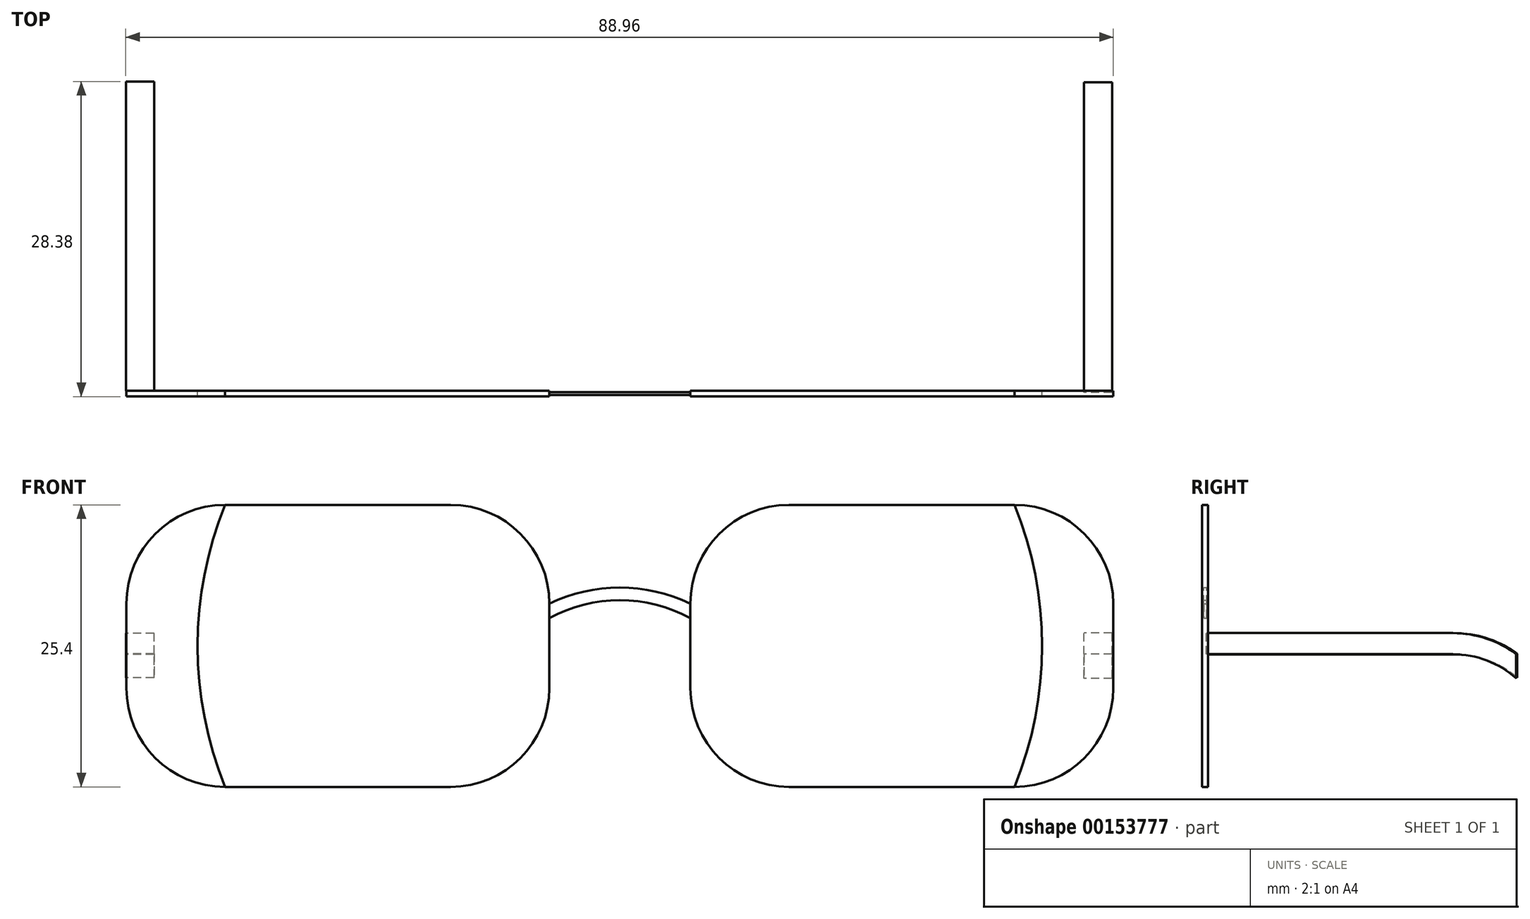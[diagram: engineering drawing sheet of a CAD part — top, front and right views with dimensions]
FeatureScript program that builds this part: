
annotation { "Feature Type Name" : "Feature", "Feature Type Description" : "" }
export const myFeature = defineFeature(function(context is Context, id is Id, definition is map)
    precondition{}
    {
        {
            var Q0;
            Q0=qCreatedBy(makeId("Front.planeOp"),FACE);
            var sketch = newSketch(context, id + "F0", { "sketchPlane" : qUnion([Q0])});
            skLineSegment(sketch, "E0.bottom", {"start": v(-55.76, 55.32) * mm, "end": v(-35.44, 55.32) * mm});
            skLineSegment(sketch, "E0.top", {"start": v(-55.76, 29.92) * mm, "end": v(-35.44, 29.92) * mm});
            skLineSegment(sketch, "E0.left", {"start": v(-64.65, 46.43) * mm, "end": v(-64.65, 38.8) * mm});
            skLineSegment(sketch, "E0.right", {"start": v(-26.55, 46.43) * mm, "end": v(-26.55, 38.8) * mm});
            skLineSegment(sketch, "E1", {"start": v(-13.85, 46.43) * mm, "end": v(-13.85, 38.8) * mm});
            skLineSegment(sketch, "E2", {"start": v(-4.96, 29.92) * mm, "end": v(15.36, 29.92) * mm});
            skLineSegment(sketch, "E3", {"start": v(24.25, 38.8) * mm, "end": v(24.25, 46.43) * mm});
            skLineSegment(sketch, "E4", {"start": v(15.36, 55.32) * mm, "end": v(-4.96, 55.32) * mm});
            skPoint(sketch, "E5.visualSharp", {"position": v(-64.65, 55.32) * mm});
            skArc(sketch, "E5.filletArc", {"start": v(-55.76, 55.32) * mm, "mid": v(-62.05, 52.71) * mm, "end": v(-64.65, 46.43) * mm});
            skPoint(sketch, "E6.visualSharp", {"position": v(-64.65, 29.92) * mm});
            skArc(sketch, "E6.filletArc", {"start": v(-64.65, 38.8) * mm, "mid": v(-62.05, 32.52) * mm, "end": v(-55.76, 29.92) * mm});
            skPoint(sketch, "E7.visualSharp", {"position": v(-26.55, 29.92) * mm});
            skArc(sketch, "E7.filletArc", {"start": v(-35.44, 29.92) * mm, "mid": v(-29.16, 32.52) * mm, "end": v(-26.55, 38.8) * mm});
            skPoint(sketch, "E8.visualSharp", {"position": v(-26.55, 55.32) * mm});
            skArc(sketch, "E8.filletArc", {"start": v(-26.55, 46.43) * mm, "mid": v(-29.16, 52.71) * mm, "end": v(-35.44, 55.32) * mm});
            skPoint(sketch, "E9.visualSharp", {"position": v(24.25, 55.32) * mm});
            skArc(sketch, "E9.filletArc", {"start": v(24.25, 54.68) * mm, "mid": v(24.06, 55.13) * mm, "end": v(23.61, 55.32) * mm});
            skPoint(sketch, "E10.visualSharp", {"position": v(-13.85, 55.32) * mm});
            skArc(sketch, "E10.filletArc", {"start": v(-4.96, 55.32) * mm, "mid": v(-11.25, 52.71) * mm, "end": v(-13.85, 46.43) * mm});
            skPoint(sketch, "E11.visualSharp", {"position": v(-13.85, 29.92) * mm});
            skArc(sketch, "E11.filletArc", {"start": v(-13.85, 38.8) * mm, "mid": v(-11.25, 32.52) * mm, "end": v(-4.96, 29.92) * mm});
            skPoint(sketch, "E12.visualSharp", {"position": v(24.25, 29.92) * mm});
            skArc(sketch, "E12.filletArc", {"start": v(15.36, 29.92) * mm, "mid": v(21.64, 32.52) * mm, "end": v(24.25, 38.8) * mm});
            skArc(sketch, "E13.filletArc", {"start": v(24.25, 46.43) * mm, "mid": v(21.64, 52.71) * mm, "end": v(15.36, 55.32) * mm});
            skArc(sketch, "E14", {"start": v(15.36, 29.92) * mm, "mid": v(17.83, 42.62) * mm, "end": v(15.36, 55.32) * mm});
            skArc(sketch, "E15", {"start": v(-55.76, 55.32) * mm, "mid": v(-58.24, 42.62) * mm, "end": v(-55.76, 29.92) * mm});
            skArc(sketch, "E16", {"start": v(-13.85, 46.43) * mm, "mid": v(-20.2, 47.87) * mm, "end": v(-26.55, 46.43) * mm});
            skPoint(sketch, "E17", {"position": v(-26.55, 45.13) * mm});
            skPoint(sketch, "E18", {"position": v(-13.85, 45.13) * mm});
            skArc(sketch, "E19", {"start": v(-13.85, 45.13) * mm, "mid": v(-20.2, 46.73) * mm, "end": v(-26.55, 45.13) * mm});
            skSolve(sketch);
        }
        {
            var Q0;
            Q0=makeQuery(id+"F0.imprint","IMPRINT",FACE,{"disambiguationData":[TD([[makeQuery(id+"F0.imprint","IMPRINT",EDGE,{"derivedFrom":sQuery(id+"F0.wireOp",EDGE,"E0.bottom")}),-1.0]])]});
            var Q1;
            Q1=makeQuery(id+"F0.imprint","IMPRINT",FACE,{"disambiguationData":[TD([[makeQuery(id+"F0.imprint","IMPRINT",EDGE,{"derivedFrom":sQuery(id+"F0.wireOp",EDGE,"E1")}),1.0]])]});
            extrude(context, id + "F1", {"entities" : qUnion([Q0, Q1]), "endBound" : BoundingType.SYMMETRIC, "depth" : 0.5 * mm});
        }
        {
            var Q0;
            Q0=makeQuery(id+"F0.imprint","IMPRINT",FACE,{"disambiguationData":[TD([[makeQuery(id+"F0.imprint","IMPRINT",EDGE,{"derivedFrom":sQuery(id+"F0.wireOp",EDGE,"E0.right")}),1.0]])]});
            extrude(context, id + "F2", {"entities" : qUnion([Q0]), "endBound" : BoundingType.SYMMETRIC, "depth" : 0.25 * mm});
        }
        {
            var Q0;
            Q0=makeQuery(id+"F0.imprint","IMPRINT",FACE,{"disambiguationData":[TD([[makeQuery(id+"F0.imprint","IMPRINT",EDGE,{"derivedFrom":sQuery(id+"F0.wireOp",EDGE,"E3")}),1.0]])]});
            var Q1;
            Q1=makeQuery(id+"F0.imprint","IMPRINT",FACE,{"disambiguationData":[TD([[makeQuery(id+"F0.imprint","IMPRINT",EDGE,{"derivedFrom":sQuery(id+"F0.wireOp",EDGE,"E0.left")}),1.0]])]});
            extrude(context, id + "F3", {"entities" : qUnion([Q0, Q1]), "endBound" : BoundingType.SYMMETRIC, "depth" : 0.53 * mm});
        }
        {
            var Q0;
            Q0=qCreatedBy(makeId("Right.planeOp"),FACE);
            var sketch = newSketch(context, id + "F4", { "sketchPlane" : qUnion([Q0])});
            skLineSegment(sketch, "E20", {"start": v(4.34, 48.02) * mm, "end": v(26.57, 48.02) * mm});
            skLineSegment(sketch, "E21", {"start": v(26.57, 48.02) * mm, "end": v(26.57, 46.12) * mm});
            skLineSegment(sketch, "E22", {"start": v(26.57, 46.12) * mm, "end": v(4.34, 46.12) * mm});
            skLineSegment(sketch, "E23", {"start": v(4.34, 46.12) * mm, "end": v(4.34, 48.02) * mm});
            skArc(sketch, "E24", {"start": v(32.28, 46.12) * mm, "mid": v(29.58, 47.53) * mm, "end": v(26.57, 48.02) * mm});
            skArc(sketch, "E25", {"start": v(32.28, 43.96) * mm, "mid": v(29.63, 45.56) * mm, "end": v(26.57, 46.12) * mm});
            skLineSegment(sketch, "E26", {"start": v(32.28, 46.12) * mm, "end": v(32.28, 43.96) * mm});
            skLineSegment(sketch, "E27", {"start": v(5.01, 39.82) * mm, "end": v(27.24, 39.82) * mm});
            skLineSegment(sketch, "E28", {"start": v(27.24, 39.82) * mm, "end": v(27.24, 37.92) * mm});
            skLineSegment(sketch, "E29", {"start": v(27.24, 37.92) * mm, "end": v(5.01, 37.92) * mm});
            skLineSegment(sketch, "E30", {"start": v(5.01, 37.92) * mm, "end": v(5.01, 39.82) * mm});
            skArc(sketch, "E31", {"start": v(32.87, 37.98) * mm, "mid": v(30.2, 39.35) * mm, "end": v(27.24, 39.82) * mm});
            skArc(sketch, "E32", {"start": v(32.87, 35.82) * mm, "mid": v(30.24, 37.38) * mm, "end": v(27.24, 37.92) * mm});
            skLineSegment(sketch, "E33", {"start": v(32.87, 37.98) * mm, "end": v(32.87, 35.82) * mm});
            skSolve(sketch);
        }
        {
            var Q0;
            Q0 = qSketchRegion(id + "F4", true);
            extrude(context, id + "F5", {"entities" : qUnion([Q0]), "endBound" : BoundingType.SYMMETRIC, "depth" : 2.54 * mm});
        }
        {
            var Q0;
            Q0=makeQuery(id+"F5.opExtrude","SWEPT_BODY",BODY,{"disambiguationData":[OSD([sQuery(id+"F4.wireOp",EDGE,"E20"),sQuery(id+"F4.wireOp",EDGE,"E22"),sQuery(id+"F4.wireOp",EDGE,"E23"),sQuery(id+"F4.wireOp",EDGE,"E24"),sQuery(id+"F4.wireOp",EDGE,"E25"),sQuery(id+"F4.wireOp",EDGE,"E26")])]});
            transform(context, id + "F6", {"entities" : qUnion([Q0]), "transformType" : TransformType.TRANSLATION_3D, "dx" : 22.86 * mm, "dy" : -4.25 * mm, "dz" : -4.25 * mm, "makeCopy" : false});
        }
        {
            var Q0;
            Q0=makeQuery(id+"F5.opExtrude","SWEPT_BODY",BODY,{"disambiguationData":[OSD([sQuery(id+"F4.wireOp",EDGE,"E27"),sQuery(id+"F4.wireOp",EDGE,"E29"),sQuery(id+"F4.wireOp",EDGE,"E30"),sQuery(id+"F4.wireOp",EDGE,"E31"),sQuery(id+"F4.wireOp",EDGE,"E32"),sQuery(id+"F4.wireOp",EDGE,"E33")])]});
            var Q1;
            Q1=sQuery(id+"F0.wireOp",VERTEX,"E7.visualSharp");
            transform(context, id + "F7", {"entities" : qUnion([Q0]), "transformType" : TransformType.TRANSLATION_3D, "dx" : -63.44 * mm, "dy" : -4.76 * mm, "dz" : 3.94 * mm, "makeCopy" : false});
        }
    });
